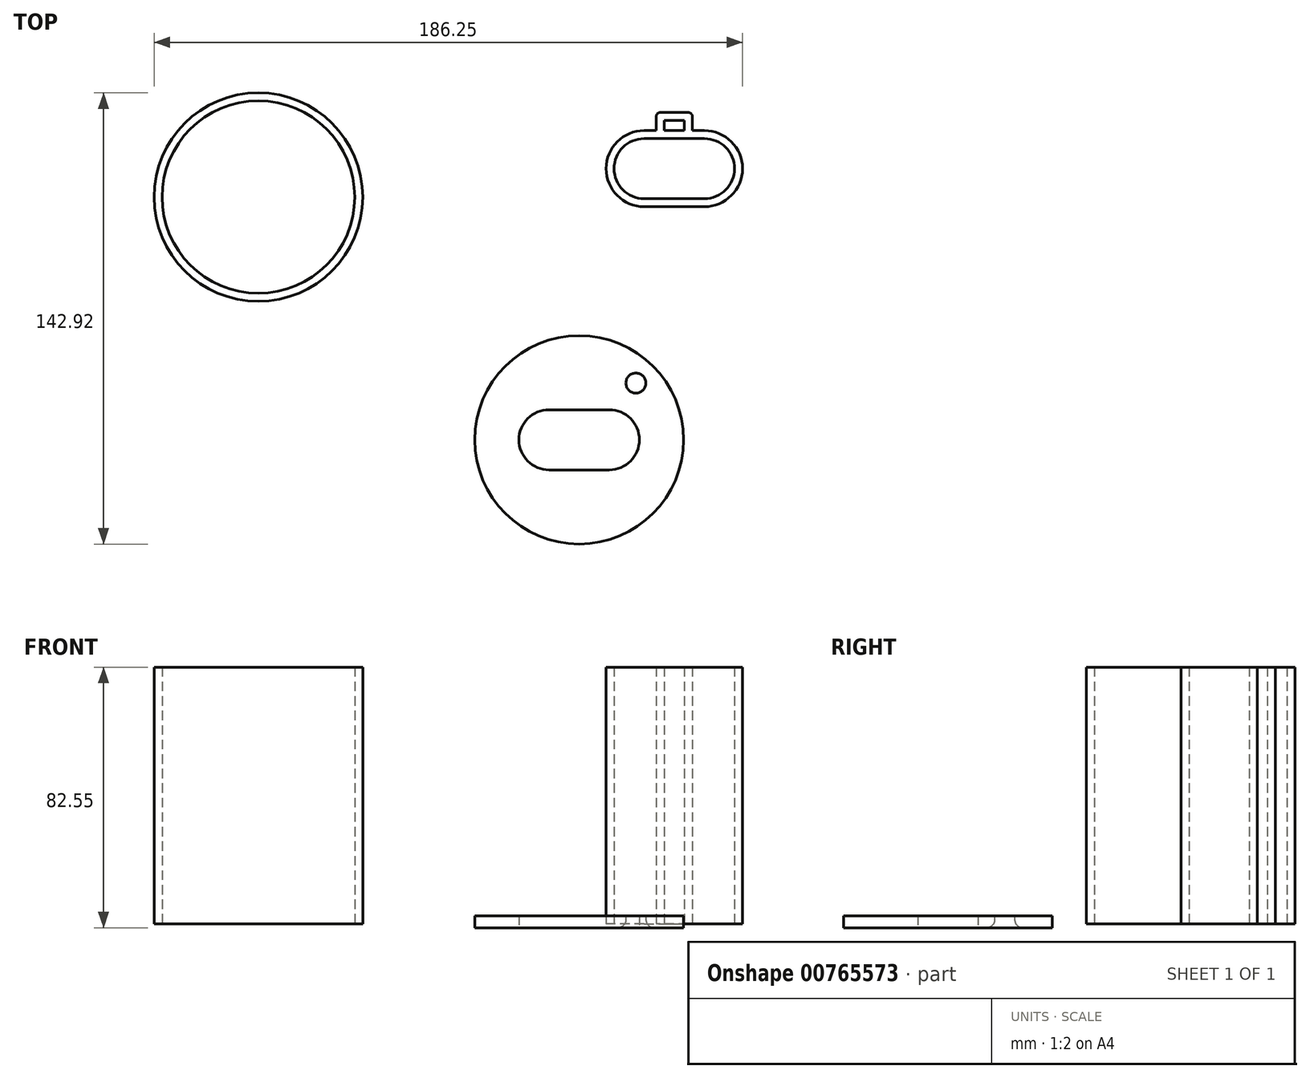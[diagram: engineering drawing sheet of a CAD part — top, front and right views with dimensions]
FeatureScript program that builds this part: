
annotation { "Feature Type Name" : "Feature", "Feature Type Description" : "" }
export const myFeature = defineFeature(function(context is Context, id is Id, definition is map)
    precondition{}
    {
        {
            var Q0;
            Q0=qCreatedBy(makeId("Top.planeOp"),FACE);
            var sketch = newSketch(context, id + "F0", { "sketchPlane" : qUnion([Q0])});
            skCircle(sketch, "E0", {"center": v(-97.84, 24.87) * mm, "radius": 33.02 * mm});
            skCircle(sketch, "E1", {"center": v(-97.84, 24.87) * mm, "radius": 30.48 * mm});
            skLineSegment(sketch, "E2.bottom", {"start": v(24.27, 43.4) * mm, "end": v(43.32, 43.4) * mm});
            skLineSegment(sketch, "E2.top", {"start": v(24.27, 24.36) * mm, "end": v(43.32, 24.36) * mm});
            skArc(sketch, "E3", {"start": v(43.32, 43.4) * mm, "mid": v(52.85, 33.88) * mm, "end": v(43.32, 24.36) * mm});
            skArc(sketch, "E4", {"start": v(24.27, 43.4) * mm, "mid": v(14.75, 33.88) * mm, "end": v(24.27, 24.36) * mm});
            skArc(sketch, "E5.0", {"start": v(43.32, 45.95) * mm, "mid": v(55.39, 33.88) * mm, "end": v(43.32, 21.82) * mm});
            skLineSegment(sketch, "E5.1", {"start": v(24.27, 45.95) * mm, "end": v(43.32, 45.95) * mm});
            skArc(sketch, "E5.2", {"start": v(24.27, 45.95) * mm, "mid": v(12.2, 33.88) * mm, "end": v(24.27, 21.82) * mm});
            skLineSegment(sketch, "E5.3", {"start": v(24.27, 21.82) * mm, "end": v(43.32, 21.82) * mm});
            skLineSegment(sketch, "E6.bottom", {"start": v(36.97, 49.12) * mm, "end": v(30.62, 49.12) * mm});
            skLineSegment(sketch, "E6.left", {"start": v(36.97, 49.12) * mm, "end": v(36.97, 45.95) * mm});
            skLineSegment(sketch, "E6.right", {"start": v(30.62, 49.12) * mm, "end": v(30.62, 45.95) * mm});
            skPoint(sketch, "E6.middle", {"position": v(33.8, 43.4) * mm});
            skPoint(sketch, "E6.top.end.orphan", {"position": v(30.62, 37.7) * mm});
            skPoint(sketch, "E7.trimOffspring.end.orphan", {"position": v(36.97, 37.7) * mm});
            skLineSegment(sketch, "E8.0", {"start": v(28.08, 50.4) * mm, "end": v(28.08, 45.95) * mm});
            skLineSegment(sketch, "E8.1", {"start": v(38.24, 51.66) * mm, "end": v(29.35, 51.66) * mm});
            skLineSegment(sketch, "E8.2", {"start": v(39.51, 50.4) * mm, "end": v(39.51, 45.95) * mm});
            skPoint(sketch, "E9.visualSharp", {"position": v(28.08, 51.66) * mm});
            skArc(sketch, "E9.filletArc", {"start": v(29.35, 51.66) * mm, "mid": v(28.46, 51.3) * mm, "end": v(28.08, 50.4) * mm});
            skPoint(sketch, "E10.visualSharp", {"position": v(39.51, 51.66) * mm});
            skArc(sketch, "E10.filletArc", {"start": v(39.51, 50.4) * mm, "mid": v(39.14, 51.3) * mm, "end": v(38.24, 51.66) * mm});
            skCircle(sketch, "E11", {"center": v(3.7, -52.01) * mm, "radius": 33.02 * mm});
            skLineSegment(sketch, "E12.bottom", {"start": v(13.22, -61.54) * mm, "end": v(-5.83, -61.54) * mm});
            skLineSegment(sketch, "E12.top", {"start": v(13.22, -42.49) * mm, "end": v(-5.83, -42.49) * mm});
            skArc(sketch, "E13", {"start": v(13.22, -42.49) * mm, "mid": v(22.74, -52.01) * mm, "end": v(13.22, -61.54) * mm});
            skArc(sketch, "E14", {"start": v(-5.83, -42.49) * mm, "mid": v(-15.36, -52.01) * mm, "end": v(-5.83, -61.54) * mm});
            skLineSegment(sketch, "E15", {"start": v(3.7, -52.01) * mm, "end": v(27.04, -28.66) * mm});
            skLineSegment(sketch, "E16", {"start": v(27.04, -28.66) * mm, "end": v(-19.66, -75.36) * mm});
            skLineSegment(sketch, "E17", {"start": v(-19.66, -75.36) * mm, "end": v(-14.27, -69.97) * mm});
            skLineSegment(sketch, "E18", {"start": v(27.04, -28.66) * mm, "end": v(21.65, -34.05) * mm});
            skCircle(sketch, "E19", {"center": v(21.65, -34.05) * mm, "radius": 3.18 * mm});
            skCircle(sketch, "E20", {"center": v(-14.27, -69.97) * mm, "radius": 3.18 * mm});
            skSolve(sketch);
        }
        {
            var Q0;
            Q0=makeQuery(id+"F0.imprint","IMPRINT",FACE,{"disambiguationData":[TD([[makeQuery(id+"F0.imprint","IMPRINT",EDGE,{"derivedFrom":sQuery(id+"F0.wireOp",EDGE,"E0")}),1.0]])]});
            var Q1;
            Q1=makeQuery(id+"F0.imprint","IMPRINT",FACE,{"disambiguationData":[TD([[makeQuery(id+"F0.imprint","IMPRINT",EDGE,{"derivedFrom":sQuery(id+"F0.wireOp",EDGE,"E6.bottom")}),-1.0]])]});
            var Q2;
            Q2=makeQuery(id+"F0.imprint","IMPRINT",FACE,{"disambiguationData":[TD([[makeQuery(id+"F0.imprint","IMPRINT",EDGE,{"derivedFrom":sQuery(id+"F0.wireOp",EDGE,"E2.bottom")}),1.0]])]});
            extrude(context, id + "F1", {"entities" : qUnion([Q0, Q1, Q2]), "depth" : 81.28 * mm, "offsetDistance" : 25.4 * mm});
        }
        {
            var Q0;
            {var subQ1=sQuery(id+"F0.wireOp",EDGE,"E12.top");Q0=makeQuery(id+"F0.imprint","IMPRINT",FACE,{"disambiguationData":[TD([[makeQuery(id+"F0.imprint","IMPRINT",EDGE,{"derivedFrom":subQ1}),-1.0]])]});}
            var Q1;
            {var subQ4=sQuery(id+"F0.wireOp",EDGE,"E12.bottom");Q1=makeQuery(id+"F0.imprint","IMPRINT",FACE,{"disambiguationData":[TD([[makeQuery(id+"F0.imprint","IMPRINT",EDGE,{"derivedFrom":subQ4}),1.0]])]});}
            var Q2;
            {var subQ0=sQuery(id+"F0.wireOp",EDGE,"E17");var subQ1=sQuery(id+"F0.wireOp",EDGE,"E16");var subQ2=makeQuery(id+"F0.imprint","INTERSECT",VERTEX,{"derivedFrom":[subQ1,subQ0]});Q2=makeQuery(id+"F0.imprint","IMPRINT",FACE,{"disambiguationData":[TD([[makeQuery(id+"F0.imprint","IMPRINT",EDGE,{"disambiguationData":[TD([[subQ2,1.0]])],"derivedFrom":subQ1}),1.0]])]});}
            var Q3;
            {var subQ0=sQuery(id+"F0.wireOp",EDGE,"E17");var subQ1=sQuery(id+"F0.wireOp",EDGE,"E16");var subQ2=makeQuery(id+"F0.imprint","INTERSECT",VERTEX,{"derivedFrom":[subQ1,subQ0]});Q3=makeQuery(id+"F0.imprint","IMPRINT",FACE,{"disambiguationData":[TD([[makeQuery(id+"F0.imprint","IMPRINT",EDGE,{"disambiguationData":[TD([[subQ2,1.0]])],"derivedFrom":subQ1}),-1.0]])]});}
            var Q4;
            {var subQ0=sQuery(id+"F0.wireOp",EDGE,"E18");var subQ1=sQuery(id+"F0.wireOp",EDGE,"E16");var subQ2=makeQuery(id+"F0.imprint","INTERSECT",VERTEX,{"derivedFrom":[subQ1,subQ0]});Q4=makeQuery(id+"F0.imprint","IMPRINT",FACE,{"disambiguationData":[TD([[makeQuery(id+"F0.imprint","IMPRINT",EDGE,{"disambiguationData":[TD([[subQ2,-1.0]])],"derivedFrom":subQ1}),1.0]])]});}
            var Q5;
            {var subQ0=sQuery(id+"F0.wireOp",EDGE,"E18");var subQ1=sQuery(id+"F0.wireOp",EDGE,"E16");var subQ2=makeQuery(id+"F0.imprint","INTERSECT",VERTEX,{"derivedFrom":[subQ1,subQ0]});Q5=makeQuery(id+"F0.imprint","IMPRINT",FACE,{"disambiguationData":[TD([[makeQuery(id+"F0.imprint","IMPRINT",EDGE,{"disambiguationData":[TD([[subQ2,-1.0]])],"derivedFrom":subQ1}),-1.0]])]});}
            extrude(context, id + "F2", {"entities" : qUnion([Q0, Q1, Q2, Q3, Q4, Q5]), "depth" : 2.54 * mm, "offsetDistance" : 25.4 * mm});
        }
        {
            var Q0;
            {var subQ0=sQuery(id+"F0.wireOp",EDGE,"E18");var subQ1=sQuery(id+"F0.wireOp",EDGE,"E16");var subQ2=makeQuery(id+"F0.imprint","INTERSECT",VERTEX,{"derivedFrom":[subQ1,subQ0]});Q0=makeQuery(id+"F0.imprint","IMPRINT",FACE,{"disambiguationData":[TD([[makeQuery(id+"F0.imprint","IMPRINT",EDGE,{"disambiguationData":[TD([[subQ2,-1.0]])],"derivedFrom":subQ1}),-1.0]])]});}
            var Q1;
            {var subQ0=sQuery(id+"F0.wireOp",EDGE,"E18");var subQ1=sQuery(id+"F0.wireOp",EDGE,"E16");var subQ2=makeQuery(id+"F0.imprint","INTERSECT",VERTEX,{"derivedFrom":[subQ1,subQ0]});Q1=makeQuery(id+"F0.imprint","IMPRINT",FACE,{"disambiguationData":[TD([[makeQuery(id+"F0.imprint","IMPRINT",EDGE,{"disambiguationData":[TD([[subQ2,-1.0]])],"derivedFrom":subQ1}),1.0]])]});}
            var Q2;
            {var subQ0=sQuery(id+"F0.wireOp",EDGE,"E17");var subQ1=sQuery(id+"F0.wireOp",EDGE,"E16");var subQ2=makeQuery(id+"F0.imprint","INTERSECT",VERTEX,{"derivedFrom":[subQ1,subQ0]});Q2=makeQuery(id+"F0.imprint","IMPRINT",FACE,{"disambiguationData":[TD([[makeQuery(id+"F0.imprint","IMPRINT",EDGE,{"disambiguationData":[TD([[subQ2,1.0]])],"derivedFrom":subQ1}),-1.0]])]});}
            var Q3;
            {var subQ0=sQuery(id+"F0.wireOp",EDGE,"E17");var subQ1=sQuery(id+"F0.wireOp",EDGE,"E16");var subQ2=makeQuery(id+"F0.imprint","INTERSECT",VERTEX,{"derivedFrom":[subQ1,subQ0]});Q3=makeQuery(id+"F0.imprint","IMPRINT",FACE,{"disambiguationData":[TD([[makeQuery(id+"F0.imprint","IMPRINT",EDGE,{"disambiguationData":[TD([[subQ2,1.0]])],"derivedFrom":subQ1}),1.0]])]});}
            extrude(context, id + "F3", {"entities" : qUnion([Q0, Q1, Q2, Q3]), "operationType" : NewBodyOperationType.ADD, "oppositeDirection" : true, "depth" : 1.27 * mm, "offsetDistance" : 25.4 * mm});
        }
        {
            var Q0;
            Q0=makeQuery(id+"F3.opExtrude","CAP_EDGE",EDGE,{"disambiguationData":[OSD([sQuery(id+"F0.wireOp",EDGE,"E19")])],"isStart":false});
            var Q1;
            Q1=makeQuery(id+"F3.opExtrude","CAP_FACE",FACE,{"disambiguationData":[OSD([sQuery(id+"F0.wireOp",EDGE,"E20")])],"isStart":false});
            var Q2;
            Q2=makeQuery(id+"F2.opExtrude","CAP_EDGE",EDGE,{"disambiguationData":[OSD([sQuery(id+"F0.wireOp",EDGE,"E13")])],"isStart":true});
            var Q3;
            Q3=makeQuery(id+"F2.opExtrude","CAP_EDGE",EDGE,{"disambiguationData":[OSD([sQuery(id+"F0.wireOp",EDGE,"E11")])],"isStart":true});
            fillet(context, id + "F4", {"entities" : qUnion([Q0, Q1, Q2, Q3]), "radius" : 2.54 * mm, "tangentPropagation" : true, "allowEdgeOverflow" : false});
        }
    });
